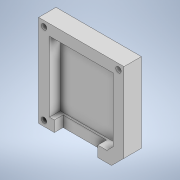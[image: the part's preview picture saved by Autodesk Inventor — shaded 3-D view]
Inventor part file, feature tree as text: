
AUTODESK INVENTOR PART (.ipt)
format: ipt  version: 2020 (Build 240168000, 168)  size: 153,088 bytes
history: native  units: mm
features: extrude x4, sketch x3, shell x1
ambient origin geometry x8: Origin, YZ Plane, XZ Plane, XY Plane, X Axis, Y Axis, Z Axis, Center Point
bodies: Solid1 (feature_tree)
feature tree (8):
  extrude  "Extrusion1"  Depth=32.25mm
  shell  "Shell2"  Thickness=5.0mm
  extrude  "Extrusion3"  Depth=5.0mm
  extrude  "Extrusion4"  TaperAngle=0.0deg  [1 undecoded]
  extrude  "Extrusion5"  Depth=20.0mm
  sketch  "Sketch3"  dims[d0=29.25mm d1=32.25mm d4=5.0mm d5=0.0mm]
  sketch  "Sketch4"  dims[d13=5.0mm d14=2.5mm]
  sketch  "Sketch5"  dims[d15=2.5mm d17=0.0mm d18=0.0mm d19=20.0mm d20=5.0mm d22=4.0mm d23=0.0mm d24=2.8mm d25=2.8mm d26=2.5mm d27=2.0mm d28=0.0mm d29=7.25mm]
note: 1 required parameter value undecoded (feature->parameter linkage not recoverable at this tier; creation-order binding heuristic only, values carry confidence <= 0.55)
